# Revit family: FAP43T-W
name_source: partatom
category: Communication Devices
revit_build: Autodesk Revit 2014 (Build: 20140709_2115(x64)
units: mm (PartAtom-declared; Revit-internal decimal feet)

## types (1)
- Two Way, Full Range, Coaxial Ceiling Loudspeaker
    100V Taps = 32, 16, 8, 4 Watts & 8Ω
    70V Taps = 32, 16, 8, 4 Watts & 8Ω
    Baffle Material = QF_Wall Paint-Gray
    Body Material = QF_Wall Paint-Gray
    Color = <By Category>
    Communication Ports = 4-Position PHX Type Connector
    Controls = Front Mounted Tap Selector Switch
    Cost = 122.99 $
    Cost MSRP = 122.99 $
    Coverage Horizontal = 110.00°
    Coverage Vertical = 110.00°
    Depth = 9.57 "
    Description = 4.5" COAXIAL IN-CEILING LOUDSPEAKER WITH 32-WATT 70V/100V TRANSFORMER, PORTED ENCLOSURE, AND SAFETY FIRST MOUNTING SYSTEM
    Dispersion Angle = 110.00°
    Enclosure Material = <By Category>
    Environmental Testing = Humidity: MIL-STD-810G / High and Low Temperature: -20° and 70° C
    Family Code (default) = LOUD SPEAKERS
    Frequency Response  = 60Hz - 20kHz
    Grill Material = QF_Wall Paint-Gray
    Height = 7.27 "
    IQ Category = SPEAKERS
    Impedance = 8
    Ingress Protection = IP-21
    Input Connectors = 4-Position PHX Type Connector
    Manufacturer = ATLAS SOUND
    Manufacturer URL = https://www.atlasied.com
    Market = Commercial, Higher Education, Emergency
    MasterFormat = 27 41 13
    MaterFormat Title = SPEAKERS
    Max Input Ratings (8Ω) = 50W Continuous, 100W Program20 Volts RMS, 40 Volts Momentary Peak
    Maximum Output = 107 dB Continuous / 113 dB Peak
    Model = FAP43T-W
    Mount Material = QF_Plastic-White-Smooth
    Mounting/Rigging Provisions = Patented Safety First Mounting System
    OmniClass Number = 23-37 17 13 19
    OmniClass Title = SPEAKERS
    Operation Mode = Non-Powered Passive
    Power Rating (RMS) = 50W Continuous, 100W Program
    Product Documentation Link = https://www.atlasied.com
    Product Page URL = TBD
    Recommended Power Amplification = 120W at 8Ω
    Recommended Signal Processing = 80Hz HPF
    Regulatory Compliance = UL Listed to Comply with UL1480, UL2043 and CSA60065. Suitable for Use in Air Handling Spaces per NFPA 70 and NFPA 90.
    SPL Max = 107
    Safety Agency Ratings = UL Listed to Comply with UL1480, UL2043 and CSA60065. Suitable for Use in Air Handling Spaces per NFPA 70 and NFPA 90.
    Safety Features = 1 Safety Hang Point
    ScheduleType |RF| = AtlasIED Master
    Sensitivity = 90
    Speaker Dispersion = 110.00°
    Speaker Type = S1
    Transformer Option = Yes
    URL = WWW.ATLASIED.COM
    Vertical Symmetry = Yes
    Warranty = 5 Year
    Weight Product = 6.23
    Width = 9.57 "

## geometry (parser evidence)
native form markers: Sweep x3
no freeform markers — native parametric forms only
